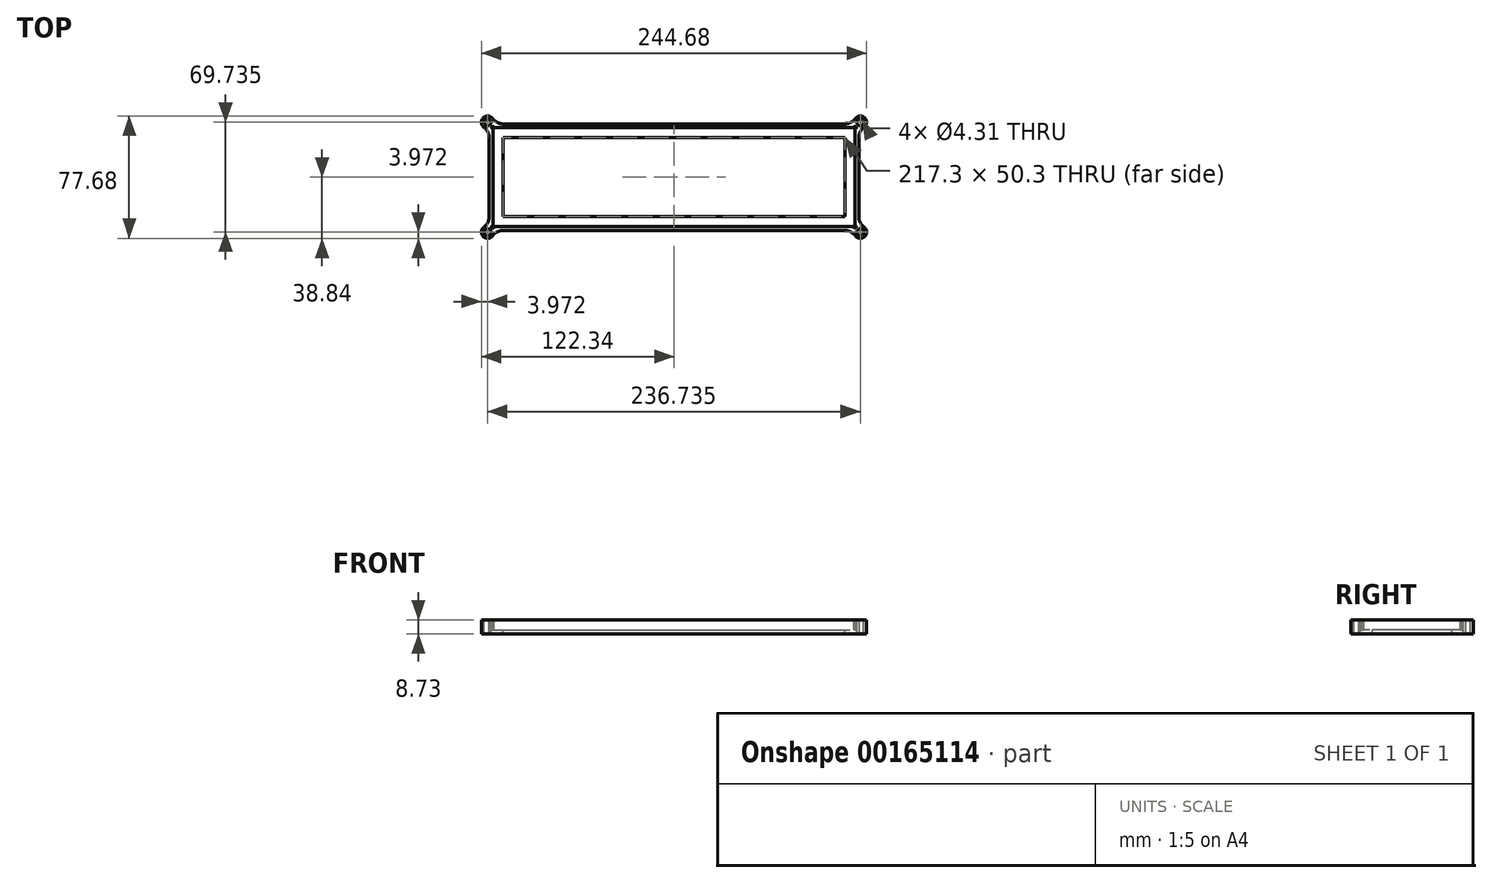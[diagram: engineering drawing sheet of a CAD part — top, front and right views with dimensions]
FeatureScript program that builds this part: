
annotation { "Feature Type Name" : "Feature", "Feature Type Description" : "" }
export const myFeature = defineFeature(function(context is Context, id is Id, definition is map)
    precondition{}
    {
        {
            var Q0;
            Q0=qCreatedBy(makeId("Top.planeOp"),FACE);
            var sketch = newSketch(context, id + "F0", { "sketchPlane" : qUnion([Q0])});
            skLineSegment(sketch, "E0.bottom", {"start": v(-115, 31.5) * mm, "end": v(115, 31.5) * mm});
            skLineSegment(sketch, "E0.top", {"start": v(-115, -31.5) * mm, "end": v(115, -31.5) * mm});
            skLineSegment(sketch, "E0.left", {"start": v(-115, 31.5) * mm, "end": v(-115, -31.5) * mm});
            skLineSegment(sketch, "E0.right", {"start": v(115, 31.5) * mm, "end": v(115, -31.5) * mm});
            skPoint(sketch, "E0.middle", {"position": v(0, 0) * mm});
            skLineSegment(sketch, "E1.bottom", {"start": v(-117.38, 33.88) * mm, "end": v(117.38, 33.88) * mm});
            skLineSegment(sketch, "E1.top", {"start": v(-117.38, -33.88) * mm, "end": v(117.38, -33.88) * mm});
            skLineSegment(sketch, "E1.left", {"start": v(-117.38, 33.88) * mm, "end": v(-117.38, -33.88) * mm});
            skLineSegment(sketch, "E1.right", {"start": v(117.38, 33.88) * mm, "end": v(117.38, -33.88) * mm});
            skLineSegment(sketch, "E2", {"start": v(-115, 31.5) * mm, "end": v(-117.38, 31.5) * mm, "construction": true});
            skLineSegment(sketch, "E3", {"start": v(-115, 31.5) * mm, "end": v(-115, 33.88) * mm, "construction": true});
            skSolve(sketch);
        }
        {
            var Q0;
            Q0 = qSketchRegion(id + "F0", true);
            extrude(context, id + "F1", {"entities" : qUnion([Q0]), "depth" : 6.35 * mm});
        }
        {
            var Q0;
            Q0=makeQuery(id+"F1.opExtrude","CAP_FACE",FACE,{"disambiguationData":[OSD([sQuery(id+"F0.wireOp",EDGE,"E0.bottom"),sQuery(id+"F0.wireOp",EDGE,"E0.top"),sQuery(id+"F0.wireOp",EDGE,"E0.left"),sQuery(id+"F0.wireOp",EDGE,"E0.right"),sQuery(id+"F0.wireOp",EDGE,"E1.bottom"),sQuery(id+"F0.wireOp",EDGE,"E1.top"),sQuery(id+"F0.wireOp",EDGE,"E1.left"),sQuery(id+"F0.wireOp",EDGE,"E1.right")])],"isStart":true});
            var sketch = newSketch(context, id + "F2", { "sketchPlane" : qUnion([Q0])});
            skLineSegment(sketch, "E4.bottom", {"start": v(-117.38, 33.88) * mm, "end": v(117.38, 33.88) * mm});
            skLineSegment(sketch, "E4.top", {"start": v(-117.38, -33.88) * mm, "end": v(117.38, -33.88) * mm});
            skLineSegment(sketch, "E4.left", {"start": v(-117.38, 33.88) * mm, "end": v(-117.38, -33.88) * mm});
            skLineSegment(sketch, "E4.right", {"start": v(117.38, 33.88) * mm, "end": v(117.38, -33.88) * mm});
            skLineSegment(sketch, "E5.bottom", {"start": v(-108.65, -25.15) * mm, "end": v(108.65, -25.15) * mm});
            skLineSegment(sketch, "E5.top", {"start": v(-108.65, 25.15) * mm, "end": v(108.65, 25.15) * mm});
            skLineSegment(sketch, "E5.left", {"start": v(-108.65, -25.15) * mm, "end": v(-108.65, 25.15) * mm});
            skLineSegment(sketch, "E5.right", {"start": v(108.65, -25.15) * mm, "end": v(108.65, 25.15) * mm});
            skPoint(sketch, "E5.middle", {"position": v(0, 0) * mm});
            skLineSegment(sketch, "E6.bottom", {"start": v(-108.65, -25.15) * mm, "end": v(-115, -25.15) * mm, "construction": true});
            skLineSegment(sketch, "E6.top", {"start": v(-108.65, -31.5) * mm, "end": v(-115, -31.5) * mm, "construction": true});
            skLineSegment(sketch, "E6.left", {"start": v(-108.65, -25.15) * mm, "end": v(-108.65, -31.5) * mm, "construction": true});
            skLineSegment(sketch, "E6.right", {"start": v(-115, -25.15) * mm, "end": v(-115, -31.5) * mm, "construction": true});
            skSolve(sketch);
        }
        {
            var Q0;
            Q0 = qSketchRegion(id + "F2", true);
            extrude(context, id + "F3", {"entities" : qUnion([Q0]), "operationType" : NewBodyOperationType.ADD, "depth" : 2.38 * mm});
        }
        {
            var Q0;
            Q0=makeQuery(id+"F1.opExtrude","CAP_FACE",FACE,{"disambiguationData":[OSD([sQuery(id+"F0.wireOp",EDGE,"E0.bottom"),sQuery(id+"F0.wireOp",EDGE,"E0.top"),sQuery(id+"F0.wireOp",EDGE,"E0.left"),sQuery(id+"F0.wireOp",EDGE,"E0.right"),sQuery(id+"F0.wireOp",EDGE,"E1.bottom"),sQuery(id+"F0.wireOp",EDGE,"E1.top"),sQuery(id+"F0.wireOp",EDGE,"E1.left"),sQuery(id+"F0.wireOp",EDGE,"E1.right")])],"isStart":false});
            var sketch = newSketch(context, id + "F4", { "sketchPlane" : qUnion([Q0])});
            skLineSegment(sketch, "E7.bottom", {"start": v(117.38, 33.88) * mm, "end": v(118.37, 33.88) * mm, "construction": true});
            skLineSegment(sketch, "E7.top", {"start": v(117.38, 34.87) * mm, "end": v(118.37, 34.87) * mm, "construction": true});
            skLineSegment(sketch, "E7.left", {"start": v(117.38, 33.88) * mm, "end": v(117.38, 34.87) * mm, "construction": true});
            skLineSegment(sketch, "E7.right", {"start": v(118.37, 33.88) * mm, "end": v(118.37, 34.87) * mm, "construction": true});
            skLineSegment(sketch, "E8", {"start": v(0, 33.88) * mm, "end": v(0, -33.88) * mm, "construction": true});
            skLineSegment(sketch, "E9.bottom", {"start": v(118.37, 34.87) * mm, "end": v(-118.37, 34.87) * mm, "construction": true});
            skLineSegment(sketch, "E9.top", {"start": v(118.37, -34.87) * mm, "end": v(-118.37, -34.87) * mm, "construction": true});
            skLineSegment(sketch, "E9.left", {"start": v(118.37, 34.87) * mm, "end": v(118.37, -34.87) * mm, "construction": true});
            skLineSegment(sketch, "E9.right", {"start": v(-118.37, 34.87) * mm, "end": v(-118.37, -34.87) * mm, "construction": true});
            skPoint(sketch, "E9.middle", {"position": v(0, 0) * mm});
            skCircle(sketch, "E10", {"center": v(118.37, 34.87) * mm, "radius": 3.97 * mm});
            skCircle(sketch, "E11", {"center": v(118.37, -34.87) * mm, "radius": 3.97 * mm});
            skCircle(sketch, "E12", {"center": v(-118.37, -34.87) * mm, "radius": 3.97 * mm});
            skCircle(sketch, "E13", {"center": v(-118.37, 34.87) * mm, "radius": 3.97 * mm});
            skCircle(sketch, "E14", {"center": v(115, 31.5) * mm, "radius": 0.8 * mm, "construction": true});
            skSolve(sketch);
        }
        {
            var Q0;
            Q0 = qSketchRegion(id + "F4", true);
            var Q1;
            Q1=makeQuery(id+"F3.opExtrude","CAP_FACE",FACE,{"disambiguationData":[OSD([sQuery(id+"F2.wireOp",EDGE,"E4.bottom"),sQuery(id+"F2.wireOp",EDGE,"E4.top"),sQuery(id+"F2.wireOp",EDGE,"E4.left"),sQuery(id+"F2.wireOp",EDGE,"E4.right")])],"isStart":false});
            extrude(context, id + "F5", {"entities" : qUnion([Q0]), "operationType" : NewBodyOperationType.ADD, "endBound" : BoundingType.UP_TO_SURFACE, "oppositeDirection" : true, "endBoundEntityFace" : qUnion([Q1]), "depth" : 25.4 * mm});
        }
        {
            var Q0;
            Q0=makeQuery(id+"F5.boolean.opBoolean","INTERSECT",EDGE,{"derivedFrom":[makeQuery(id+"F3.boolean.opBoolean","MERGE",FACE,{"derivedFrom":[makeQuery(id+"F1.opExtrude","SWEPT_FACE",FACE,{"disambiguationData":[OSD([sQuery(id+"F0.wireOp",EDGE,"E1.bottom")])]}),makeQuery(id+"F3.opExtrude","SWEPT_FACE",FACE,{"disambiguationData":[OSD([sQuery(id+"F2.wireOp",EDGE,"E4.top")])]})]}),makeQuery(id+"F5.opExtrude","SWEPT_FACE",FACE,{"disambiguationData":[OSD([sQuery(id+"F4.wireOp",EDGE,"E10")])]})]});
            var Q1;
            Q1=makeQuery(id+"F5.boolean.opBoolean","INTERSECT",EDGE,{"derivedFrom":[makeQuery(id+"F3.boolean.opBoolean","MERGE",FACE,{"derivedFrom":[makeQuery(id+"F1.opExtrude","SWEPT_FACE",FACE,{"disambiguationData":[OSD([sQuery(id+"F0.wireOp",EDGE,"E1.right")])]}),makeQuery(id+"F3.opExtrude","SWEPT_FACE",FACE,{"disambiguationData":[OSD([sQuery(id+"F2.wireOp",EDGE,"E4.right")])]})]}),makeQuery(id+"F5.opExtrude","SWEPT_FACE",FACE,{"disambiguationData":[OSD([sQuery(id+"F4.wireOp",EDGE,"E10")])]})]});
            var Q2;
            Q2=makeQuery(id+"F5.boolean.opBoolean","INTERSECT",EDGE,{"derivedFrom":[makeQuery(id+"F3.boolean.opBoolean","MERGE",FACE,{"derivedFrom":[makeQuery(id+"F1.opExtrude","SWEPT_FACE",FACE,{"disambiguationData":[OSD([sQuery(id+"F0.wireOp",EDGE,"E1.right")])]}),makeQuery(id+"F3.opExtrude","SWEPT_FACE",FACE,{"disambiguationData":[OSD([sQuery(id+"F2.wireOp",EDGE,"E4.right")])]})]}),makeQuery(id+"F5.opExtrude","SWEPT_FACE",FACE,{"disambiguationData":[OSD([sQuery(id+"F4.wireOp",EDGE,"E11")])]})]});
            var Q3;
            Q3=makeQuery(id+"F5.boolean.opBoolean","INTERSECT",EDGE,{"derivedFrom":[makeQuery(id+"F3.boolean.opBoolean","MERGE",FACE,{"derivedFrom":[makeQuery(id+"F1.opExtrude","SWEPT_FACE",FACE,{"disambiguationData":[OSD([sQuery(id+"F0.wireOp",EDGE,"E1.top")])]}),makeQuery(id+"F3.opExtrude","SWEPT_FACE",FACE,{"disambiguationData":[OSD([sQuery(id+"F2.wireOp",EDGE,"E4.bottom")])]})]}),makeQuery(id+"F5.opExtrude","SWEPT_FACE",FACE,{"disambiguationData":[OSD([sQuery(id+"F4.wireOp",EDGE,"E11")])]})]});
            var Q4;
            Q4=makeQuery(id+"F5.boolean.opBoolean","INTERSECT",EDGE,{"derivedFrom":[makeQuery(id+"F3.boolean.opBoolean","MERGE",FACE,{"derivedFrom":[makeQuery(id+"F1.opExtrude","SWEPT_FACE",FACE,{"disambiguationData":[OSD([sQuery(id+"F0.wireOp",EDGE,"E1.left")])]}),makeQuery(id+"F3.opExtrude","SWEPT_FACE",FACE,{"disambiguationData":[OSD([sQuery(id+"F2.wireOp",EDGE,"E4.left")])]})]}),makeQuery(id+"F5.opExtrude","SWEPT_FACE",FACE,{"disambiguationData":[OSD([sQuery(id+"F4.wireOp",EDGE,"E12")])]})]});
            var Q5;
            Q5=makeQuery(id+"F5.boolean.opBoolean","INTERSECT",EDGE,{"derivedFrom":[makeQuery(id+"F3.boolean.opBoolean","MERGE",FACE,{"derivedFrom":[makeQuery(id+"F1.opExtrude","SWEPT_FACE",FACE,{"disambiguationData":[OSD([sQuery(id+"F0.wireOp",EDGE,"E1.top")])]}),makeQuery(id+"F3.opExtrude","SWEPT_FACE",FACE,{"disambiguationData":[OSD([sQuery(id+"F2.wireOp",EDGE,"E4.bottom")])]})]}),makeQuery(id+"F5.opExtrude","SWEPT_FACE",FACE,{"disambiguationData":[OSD([sQuery(id+"F4.wireOp",EDGE,"E12")])]})]});
            var Q6;
            Q6=makeQuery(id+"F5.boolean.opBoolean","INTERSECT",EDGE,{"derivedFrom":[makeQuery(id+"F3.boolean.opBoolean","MERGE",FACE,{"derivedFrom":[makeQuery(id+"F1.opExtrude","SWEPT_FACE",FACE,{"disambiguationData":[OSD([sQuery(id+"F0.wireOp",EDGE,"E1.bottom")])]}),makeQuery(id+"F3.opExtrude","SWEPT_FACE",FACE,{"disambiguationData":[OSD([sQuery(id+"F2.wireOp",EDGE,"E4.top")])]})]}),makeQuery(id+"F5.opExtrude","SWEPT_FACE",FACE,{"disambiguationData":[OSD([sQuery(id+"F4.wireOp",EDGE,"E13")])]})]});
            var Q7;
            Q7=makeQuery(id+"F5.boolean.opBoolean","INTERSECT",EDGE,{"derivedFrom":[makeQuery(id+"F3.boolean.opBoolean","MERGE",FACE,{"derivedFrom":[makeQuery(id+"F1.opExtrude","SWEPT_FACE",FACE,{"disambiguationData":[OSD([sQuery(id+"F0.wireOp",EDGE,"E1.left")])]}),makeQuery(id+"F3.opExtrude","SWEPT_FACE",FACE,{"disambiguationData":[OSD([sQuery(id+"F2.wireOp",EDGE,"E4.left")])]})]}),makeQuery(id+"F5.opExtrude","SWEPT_FACE",FACE,{"disambiguationData":[OSD([sQuery(id+"F4.wireOp",EDGE,"E13")])]})]});
            fillet(context, id + "F6", {"entities" : qUnion([Q0, Q1, Q2, Q3, Q4, Q5, Q6, Q7]), "radius" : 7.94 * mm, "tangentPropagation" : true, "allowEdgeOverflow" : false});
        }
        {
            var Q0;
            Q0=makeQuery(id+"F5.boolean.opBoolean","MERGE",FACE,{"derivedFrom":[makeQuery(id+"F1.opExtrude","CAP_FACE",FACE,{"disambiguationData":[OSD([sQuery(id+"F0.wireOp",EDGE,"E0.bottom"),sQuery(id+"F0.wireOp",EDGE,"E0.top"),sQuery(id+"F0.wireOp",EDGE,"E0.left"),sQuery(id+"F0.wireOp",EDGE,"E0.right"),sQuery(id+"F0.wireOp",EDGE,"E1.bottom"),sQuery(id+"F0.wireOp",EDGE,"E1.top"),sQuery(id+"F0.wireOp",EDGE,"E1.left"),sQuery(id+"F0.wireOp",EDGE,"E1.right")])],"isStart":false}),makeQuery(id+"F5.opExtrude","CAP_FACE",FACE,{"disambiguationData":[OSD([sQuery(id+"F4.wireOp",EDGE,"E10")])],"isStart":true}),makeQuery(id+"F5.opExtrude","CAP_FACE",FACE,{"disambiguationData":[OSD([sQuery(id+"F4.wireOp",EDGE,"E11")])],"isStart":true}),makeQuery(id+"F5.opExtrude","CAP_FACE",FACE,{"disambiguationData":[OSD([sQuery(id+"F4.wireOp",EDGE,"E12")])],"isStart":true}),makeQuery(id+"F5.opExtrude","CAP_FACE",FACE,{"disambiguationData":[OSD([sQuery(id+"F4.wireOp",EDGE,"E13")])],"isStart":true})]});
            var sketch = newSketch(context, id + "F7", { "sketchPlane" : qUnion([Q0])});
            skCircle(sketch, "E15", {"center": v(118.37, 34.87) * mm, "radius": 2.15 * mm});
            skCircle(sketch, "E16", {"center": v(118.37, -34.87) * mm, "radius": 2.15 * mm});
            skCircle(sketch, "E17", {"center": v(-118.37, 34.87) * mm, "radius": 2.15 * mm});
            skCircle(sketch, "E18", {"center": v(-118.37, -34.87) * mm, "radius": 2.15 * mm});
            skSolve(sketch);
        }
        {
            var Q0;
            Q0 = qSketchRegion(id + "F7", true);
            var Q1;
            Q1=makeQuery(id+"F5.boolean.opBoolean","MERGE",FACE,{"derivedFrom":[makeQuery(id+"F3.opExtrude","CAP_FACE",FACE,{"disambiguationData":[OSD([sQuery(id+"F2.wireOp",EDGE,"E4.bottom"),sQuery(id+"F2.wireOp",EDGE,"E4.top"),sQuery(id+"F2.wireOp",EDGE,"E4.left"),sQuery(id+"F2.wireOp",EDGE,"E4.right"),sQuery(id+"F2.wireOp",EDGE,"E5.bottom"),sQuery(id+"F2.wireOp",EDGE,"E5.top"),sQuery(id+"F2.wireOp",EDGE,"E5.left"),sQuery(id+"F2.wireOp",EDGE,"E5.right")])],"isStart":false}),makeQuery(id+"F5.opExtrude","CAP_FACE",FACE,{"disambiguationData":[OSD([sQuery(id+"F4.wireOp",EDGE,"E10")])],"isStart":false}),makeQuery(id+"F5.opExtrude","CAP_FACE",FACE,{"disambiguationData":[OSD([sQuery(id+"F4.wireOp",EDGE,"E11")])],"isStart":false}),makeQuery(id+"F5.opExtrude","CAP_FACE",FACE,{"disambiguationData":[OSD([sQuery(id+"F4.wireOp",EDGE,"E12")])],"isStart":false}),makeQuery(id+"F5.opExtrude","CAP_FACE",FACE,{"disambiguationData":[OSD([sQuery(id+"F4.wireOp",EDGE,"E13")])],"isStart":false})]});
            extrude(context, id + "F8", {"entities" : qUnion([Q0]), "operationType" : NewBodyOperationType.REMOVE, "endBound" : BoundingType.UP_TO_SURFACE, "oppositeDirection" : true, "endBoundEntityFace" : qUnion([Q1]), "depth" : 25.4 * mm});
        }
        {
            var Q0;
            Q0=makeQuery(id+"F5.boolean.opBoolean","MERGE",FACE,{"derivedFrom":[makeQuery(id+"F1.opExtrude","CAP_FACE",FACE,{"disambiguationData":[OSD([sQuery(id+"F0.wireOp",EDGE,"E0.bottom"),sQuery(id+"F0.wireOp",EDGE,"E0.top"),sQuery(id+"F0.wireOp",EDGE,"E0.left"),sQuery(id+"F0.wireOp",EDGE,"E0.right"),sQuery(id+"F0.wireOp",EDGE,"E1.bottom"),sQuery(id+"F0.wireOp",EDGE,"E1.top"),sQuery(id+"F0.wireOp",EDGE,"E1.left"),sQuery(id+"F0.wireOp",EDGE,"E1.right")])],"isStart":false}),makeQuery(id+"F5.opExtrude","CAP_FACE",FACE,{"disambiguationData":[OSD([sQuery(id+"F4.wireOp",EDGE,"E10")])],"isStart":true}),makeQuery(id+"F5.opExtrude","CAP_FACE",FACE,{"disambiguationData":[OSD([sQuery(id+"F4.wireOp",EDGE,"E11")])],"isStart":true}),makeQuery(id+"F5.opExtrude","CAP_FACE",FACE,{"disambiguationData":[OSD([sQuery(id+"F4.wireOp",EDGE,"E12")])],"isStart":true}),makeQuery(id+"F5.opExtrude","CAP_FACE",FACE,{"disambiguationData":[OSD([sQuery(id+"F4.wireOp",EDGE,"E13")])],"isStart":true})]});
            var sketch = newSketch(context, id + "F9", { "sketchPlane" : qUnion([Q0])});
            skCircle(sketch, "E19", {"center": v(-115, 31.5) * mm, "radius": 0.8 * mm});
            skCircle(sketch, "E20", {"center": v(-115, -31.5) * mm, "radius": 0.8 * mm});
            skCircle(sketch, "E21", {"center": v(115, -31.5) * mm, "radius": 0.8 * mm});
            skCircle(sketch, "E22", {"center": v(115, 31.5) * mm, "radius": 0.8 * mm});
            skSolve(sketch);
        }
        {
            var Q0;
            Q0 = qSketchRegion(id + "F9", true);
            var Q1;
            Q1=makeQuery(id+"F3.opExtrude","CAP_FACE",FACE,{"disambiguationData":[OSD([sQuery(id+"F2.wireOp",EDGE,"E4.bottom"),sQuery(id+"F2.wireOp",EDGE,"E4.top"),sQuery(id+"F2.wireOp",EDGE,"E4.left"),sQuery(id+"F2.wireOp",EDGE,"E4.right")])],"isStart":true});
            extrude(context, id + "F10", {"entities" : qUnion([Q0]), "operationType" : NewBodyOperationType.REMOVE, "endBound" : BoundingType.UP_TO_SURFACE, "oppositeDirection" : true, "endBoundEntityFace" : qUnion([Q1]), "depth" : 25.4 * mm});
        }
    });
